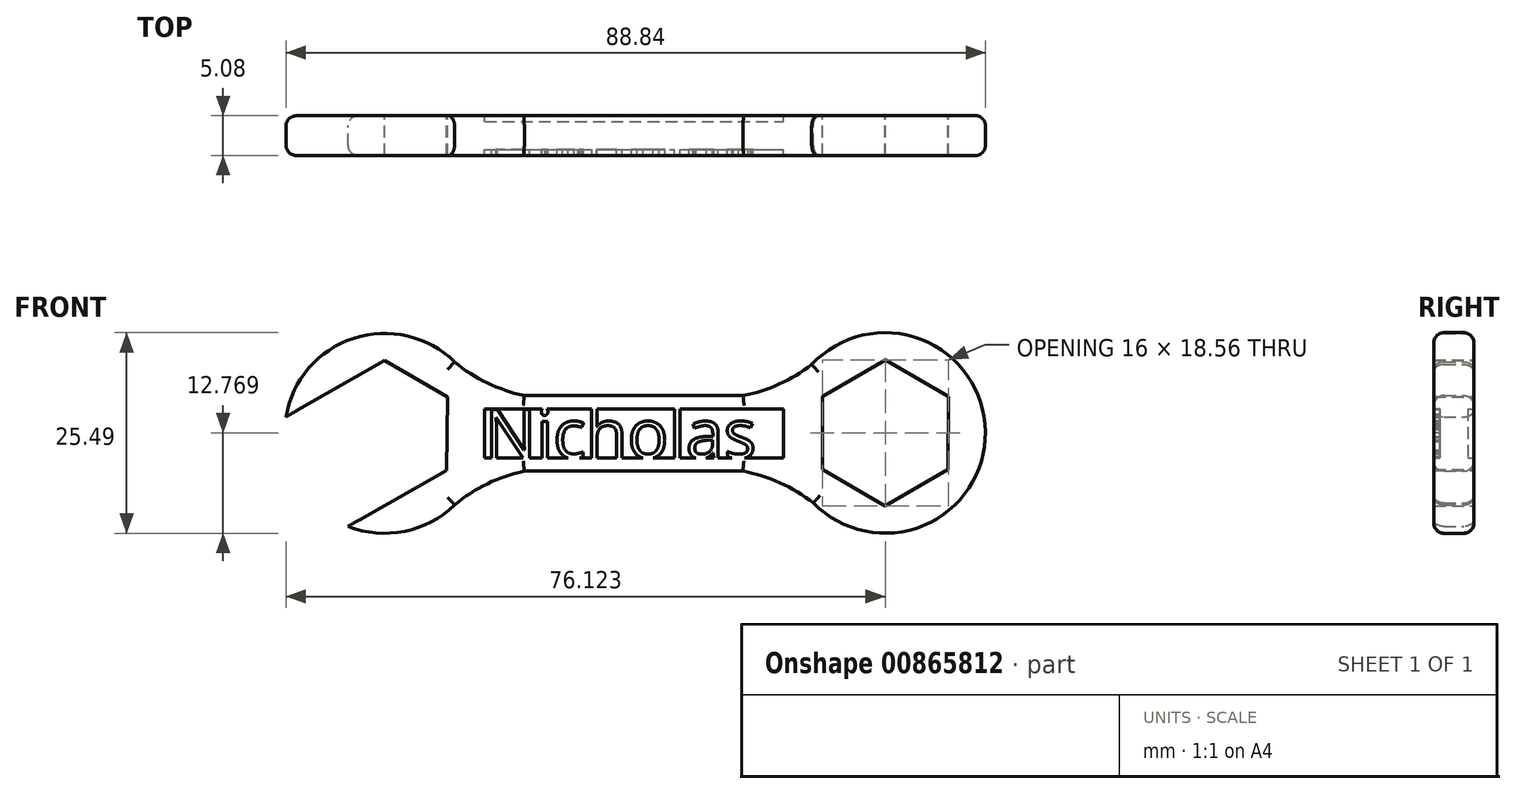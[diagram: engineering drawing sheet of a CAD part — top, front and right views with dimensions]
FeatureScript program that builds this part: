
annotation { "Feature Type Name" : "Feature", "Feature Type Description" : "" }
export const myFeature = defineFeature(function(context is Context, id is Id, definition is map)
    precondition{}
    {
        {
            var Q0;
            Q0=qCreatedBy(makeId("Front.planeOp"),FACE);
            var sketch = newSketch(context, id + "F0", { "sketchPlane" : qUnion([Q0])});
            skLineSegment(sketch, "E0.bottom", {"start": v(0, 28.47) * mm, "end": v(27.8, 28.47) * mm});
            skLineSegment(sketch, "E0.top", {"start": v(0, 18.87) * mm, "end": v(27.77, 18.87) * mm});
            skArc(sketch, "E1", {"start": v(-8.87, 32.75) * mm, "mid": v(-21.68, 35.74) * mm, "end": v(-30.27, 25.77) * mm});
            skArc(sketch, "E2", {"start": v(-8.87, 32.75) * mm, "mid": v(-4.7, 30.07) * mm, "end": v(0, 28.47) * mm});
            skArc(sketch, "E3", {"start": v(0, 18.87) * mm, "mid": v(-4.7, 17.27) * mm, "end": v(-8.87, 14.6) * mm});
            skArc(sketch, "E4", {"start": v(36.72, 14.82) * mm, "mid": v(58.57, 23.88) * mm, "end": v(36.51, 32.41) * mm});
            skArc(sketch, "E5", {"start": v(27.8, 28.47) * mm, "mid": v(32.43, 29.95) * mm, "end": v(36.6, 32.47) * mm});
            skArc(sketch, "E6", {"start": v(36.72, 14.82) * mm, "mid": v(32.49, 17.39) * mm, "end": v(27.77, 18.87) * mm});
            skPoint(sketch, "E7.orphan", {"position": v(-17.75, 28.47) * mm});
            skPoint(sketch, "E8.orphan", {"position": v(-17.75, 18.87) * mm});
            skPoint(sketch, "E9.orphan", {"position": v(45.83, 28.58) * mm});
            skPoint(sketch, "E10.orphan", {"position": v(45.83, 18.87) * mm});
            skLineSegment(sketch, "E11.1", {"start": v(-30.27, 25.77) * mm, "end": v(-17.77, 32.93) * mm});
            skLineSegment(sketch, "E11.2", {"start": v(-17.77, 32.93) * mm, "end": v(-9.74, 28.3) * mm});
            skLineSegment(sketch, "E11.3", {"start": v(-9.74, 28.3) * mm, "end": v(-9.88, 18.97) * mm});
            skLineSegment(sketch, "E11.4", {"start": v(-9.88, 18.97) * mm, "end": v(-22.4, 11.85) * mm});
            skPoint(sketch, "E11.0.midPoint", {"position": v(-25.75, 23.67) * mm});
            skArc(sketch, "E12.trimOffspring", {"start": v(-22.4, 11.85) * mm, "mid": v(-15.23, 11.22) * mm, "end": v(-8.87, 14.6) * mm});
            skLineSegment(sketch, "E13.0", {"start": v(37.85, 19.06) * mm, "end": v(37.85, 28.39) * mm});
            skLineSegment(sketch, "E13.1", {"start": v(37.85, 28.39) * mm, "end": v(45.88, 33.02) * mm});
            skLineSegment(sketch, "E13.2", {"start": v(45.88, 33.02) * mm, "end": v(53.86, 28.39) * mm});
            skLineSegment(sketch, "E13.3", {"start": v(53.86, 28.39) * mm, "end": v(53.8, 19.06) * mm});
            skLineSegment(sketch, "E13.4", {"start": v(53.8, 19.06) * mm, "end": v(45.83, 14.46) * mm});
            skLineSegment(sketch, "E13.5", {"start": v(45.83, 14.46) * mm, "end": v(37.85, 19.06) * mm});
            skPoint(sketch, "E13.0.midPoint", {"position": v(37.85, 23.72) * mm});
            skLineSegment(sketch, "E14.bottom", {"start": v(-5.04, 26.76) * mm, "end": v(32.9, 26.76) * mm});
            skLineSegment(sketch, "E14.top", {"start": v(-5.04, 20.53) * mm, "end": v(32.9, 20.53) * mm});
            skLineSegment(sketch, "E14.left", {"start": v(-5.04, 26.76) * mm, "end": v(-5.04, 20.53) * mm});
            skLineSegment(sketch, "E14.right", {"start": v(32.9, 26.76) * mm, "end": v(32.9, 20.53) * mm});
            skSolve(sketch);
        }
        {
            var Q0;
            Q0 = qSketchRegion(id + "F0", true);
            extrude(context, id + "F1", {"entities" : qUnion([Q0]), "depth" : 5.08 * mm, "offsetDistance" : 25.4 * mm});
        }
        {
            var Q0;
            Q0=makeQuery(id+"F1.opExtrude","CAP_EDGE",EDGE,{"disambiguationData":[OSD([sQuery(id+"F0.wireOp",EDGE,"E0.bottom")])],"isStart":false});
            var Q1;
            Q1=makeQuery(id+"F1.opExtrude","CAP_EDGE",EDGE,{"disambiguationData":[OSD([sQuery(id+"F0.wireOp",EDGE,"E2")])],"isStart":false});
            var Q2;
            Q2=makeQuery(id+"F1.opExtrude","CAP_EDGE",EDGE,{"disambiguationData":[OSD([sQuery(id+"F0.wireOp",EDGE,"E1")])],"isStart":false});
            var Q3;
            Q3=makeQuery(id+"F1.opExtrude","CAP_EDGE",EDGE,{"disambiguationData":[OSD([sQuery(id+"F0.wireOp",EDGE,"E3")])],"isStart":false});
            var Q4;
            Q4=makeQuery(id+"F1.opExtrude","CAP_EDGE",EDGE,{"disambiguationData":[OSD([sQuery(id+"F0.wireOp",EDGE,"E12.trimOffspring")])],"isStart":false});
            var Q5;
            Q5=makeQuery(id+"F1.opExtrude","CAP_EDGE",EDGE,{"disambiguationData":[OSD([sQuery(id+"F0.wireOp",EDGE,"E0.top")])],"isStart":false});
            var Q6;
            Q6=makeQuery(id+"F1.opExtrude","CAP_EDGE",EDGE,{"disambiguationData":[OSD([sQuery(id+"F0.wireOp",EDGE,"E6")])],"isStart":false});
            var Q7;
            Q7=makeQuery(id+"F1.opExtrude","CAP_EDGE",EDGE,{"disambiguationData":[OSD([sQuery(id+"F0.wireOp",EDGE,"E4")])],"isStart":false});
            var Q8;
            Q8=makeQuery(id+"F1.opExtrude","CAP_EDGE",EDGE,{"disambiguationData":[OSD([sQuery(id+"F0.wireOp",EDGE,"E5")])],"isStart":false});
            fillet(context, id + "F2", {"entities" : qUnion([Q0, Q1, Q2, Q3, Q4, Q5, Q6, Q7, Q8]), "radius" : 1.27 * mm, "tangentPropagation" : true, "allowEdgeOverflow" : false});
        }
        {
            var Q0;
            Q0=makeQuery(id+"F1.opExtrude","CAP_EDGE",EDGE,{"disambiguationData":[OSD([sQuery(id+"F0.wireOp",EDGE,"E0.bottom")])],"isStart":true});
            var Q1;
            Q1=makeQuery(id+"F1.opExtrude","CAP_EDGE",EDGE,{"disambiguationData":[OSD([sQuery(id+"F0.wireOp",EDGE,"E5")])],"isStart":true});
            var Q2;
            Q2=makeQuery(id+"F1.opExtrude","CAP_EDGE",EDGE,{"disambiguationData":[OSD([sQuery(id+"F0.wireOp",EDGE,"E4")])],"isStart":true});
            var Q3;
            Q3=makeQuery(id+"F1.opExtrude","CAP_EDGE",EDGE,{"disambiguationData":[OSD([sQuery(id+"F0.wireOp",EDGE,"E6")])],"isStart":true});
            var Q4;
            Q4=makeQuery(id+"F1.opExtrude","CAP_EDGE",EDGE,{"disambiguationData":[OSD([sQuery(id+"F0.wireOp",EDGE,"E0.top")])],"isStart":true});
            var Q5;
            Q5=makeQuery(id+"F1.opExtrude","CAP_EDGE",EDGE,{"disambiguationData":[OSD([sQuery(id+"F0.wireOp",EDGE,"E3")])],"isStart":true});
            var Q6;
            Q6=makeQuery(id+"F1.opExtrude","CAP_EDGE",EDGE,{"disambiguationData":[OSD([sQuery(id+"F0.wireOp",EDGE,"E2")])],"isStart":true});
            var Q7;
            Q7=makeQuery(id+"F1.opExtrude","CAP_EDGE",EDGE,{"disambiguationData":[OSD([sQuery(id+"F0.wireOp",EDGE,"E1")])],"isStart":true});
            var Q8;
            Q8=makeQuery(id+"F1.opExtrude","CAP_EDGE",EDGE,{"disambiguationData":[OSD([sQuery(id+"F0.wireOp",EDGE,"E12.trimOffspring")])],"isStart":true});
            fillet(context, id + "F3", {"entities" : qUnion([Q0, Q1, Q2, Q3, Q4, Q5, Q6, Q7, Q8]), "radius" : 1.27 * mm, "tangentPropagation" : true, "allowEdgeOverflow" : false});
        }
        {
            var Q0;
            Q0=makeQuery(id+"F0.imprint","IMPRINT",FACE,{"disambiguationData":[TD([[makeQuery(id+"F0.imprint","IMPRINT",EDGE,{"derivedFrom":sQuery(id+"F0.wireOp",EDGE,"E14.bottom")}),-1.0]])]});
            extrude(context, id + "F4", {"entities" : qUnion([Q0]), "operationType" : NewBodyOperationType.ADD, "depth" : 4.32 * mm, "offsetDistance" : 25.4 * mm, "hasSecondDirection" : true, "secondDirectionOppositeDirection" : false, "secondDirectionDepth" : 0.76 * mm});
        }
        {
            var Q0;
            Q0=makeQuery(id+"F4.opExtrude","CAP_FACE",FACE,{"disambiguationData":[OSD([sQuery(id+"F0.wireOp",EDGE,"E14.bottom"),sQuery(id+"F0.wireOp",EDGE,"E14.top"),sQuery(id+"F0.wireOp",EDGE,"E14.left"),sQuery(id+"F0.wireOp",EDGE,"E14.right")])],"isStart":false});
            var sketch = newSketch(context, id + "F5", { "sketchPlane" : qUnion([Q0])});
            skText(sketch, "E15", { "text": "Nicholas", "fontName": "OpenSans-Regular.ttf"});
            const initialGuessF5  = {"E15": [-0.00504, 0.02053, 1, 0, 0.00623]};
            skSetInitialGuess(sketch, initialGuessF5);
            skSolve(sketch);
        }
        {
            var Q0;
            Q0 = qSketchRegion(id + "F5", true);
            extrude(context, id + "F6", {"entities" : qUnion([Q0]), "operationType" : NewBodyOperationType.ADD, "depth" : 0.76 * mm, "offsetDistance" : 25.4 * mm});
        }
    });
